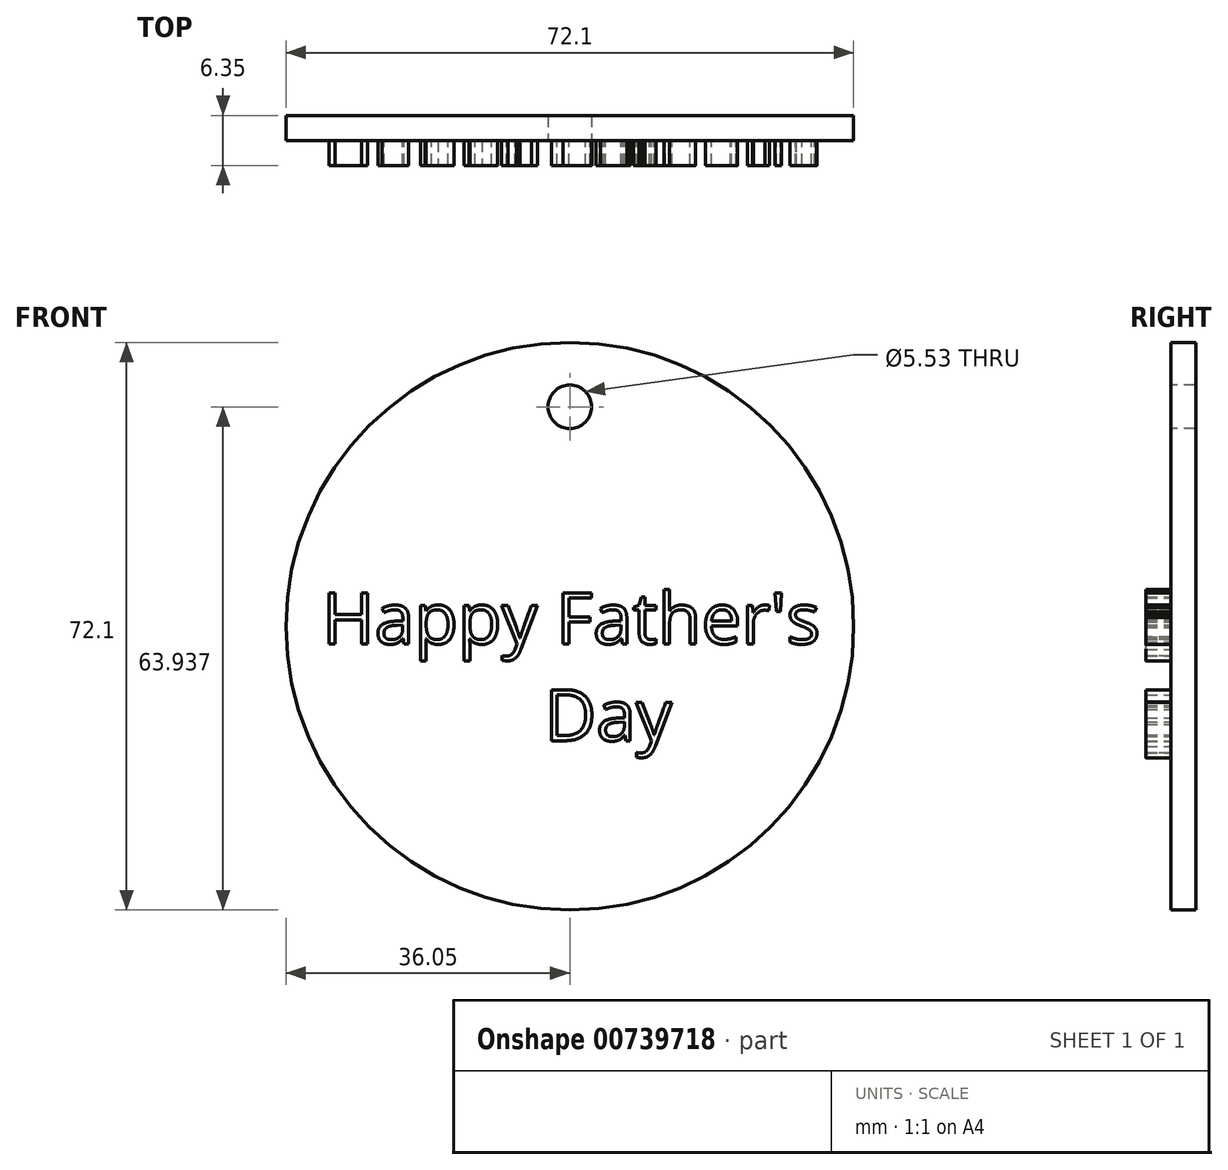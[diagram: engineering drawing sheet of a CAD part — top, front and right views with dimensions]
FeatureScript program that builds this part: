
annotation { "Feature Type Name" : "Feature", "Feature Type Description" : "" }
export const myFeature = defineFeature(function(context is Context, id is Id, definition is map)
    precondition{}
    {
        {
            var Q0;
            Q0=qCreatedBy(makeId("Front.planeOp"),FACE);
            var sketch = newSketch(context, id + "F0", { "sketchPlane" : qUnion([Q0])});
            skCircle(sketch, "E0", {"center": v(0, 0) * mm, "radius": 36.05 * mm});
            skSolve(sketch);
        }
        {
            var Q0;
            Q0=makeQuery(id+"F0.imprint","IMPRINT",FACE,{"disambiguationData":[TD([[makeQuery(id+"F0.imprint","IMPRINT",EDGE,{"derivedFrom":sQuery(id+"F0.wireOp",EDGE,"E0")}),1.0]])]});
            extrude(context, id + "F1", {"entities" : qUnion([Q0]), "depth" : 3.17 * mm, "offsetDistance" : 25.4 * mm});
        }
        {
            var Q0;
            Q0=makeQuery(id+"F1.opExtrude","CAP_FACE",FACE,{"disambiguationData":[OSD([sQuery(id+"F0.wireOp",EDGE,"E0")])],"isStart":false});
            var sketch = newSketch(context, id + "F2", { "sketchPlane" : qUnion([Q0])});
            skText(sketch, "E1", { "text": "Happy Father\'s\n            Day", "fontName": "OpenSans-Regular.ttf"});
            const initialGuessF2  = {"E1": [-0.03148, -0.00222, 1, 0, 0.00652]};
            skSetInitialGuess(sketch, initialGuessF2);
            skSolve(sketch);
        }
        {
            var Q0;
            Q0 = qSketchRegion(id + "F2", true);
            extrude(context, id + "F3", {"entities" : qUnion([Q0]), "operationType" : NewBodyOperationType.ADD, "depth" : 3.17 * mm, "offsetDistance" : 25.4 * mm});
        }
        {
            var Q0;
            {var subQ0=sQuery(id+"F0.wireOp",EDGE,"E0");Q0=makeQuery(id+"F3.boolean.opBoolean","SPLIT",FACE,{"disambiguationData":[TD([makeQuery(id+"F1.opExtrude","SWEPT_FACE",FACE,{"disambiguationData":[OSD([subQ0])]})])],"derivedFrom":makeQuery(id+"F1.opExtrude","CAP_FACE",FACE,{"disambiguationData":[OSD([subQ0])],"isStart":false})});}
            var sketch = newSketch(context, id + "F4", { "sketchPlane" : qUnion([Q0])});
            skCircle(sketch, "E2", {"center": v(0, 27.89) * mm, "radius": 2.77 * mm});
            skSolve(sketch);
        }
        {
            var Q0;
            Q0 = qSketchRegion(id + "F4", true);
            extrude(context, id + "F5", {"entities" : qUnion([Q0]), "operationType" : NewBodyOperationType.REMOVE, "endBound" : BoundingType.SYMMETRIC, "oppositeDirection" : true, "depth" : 25.4 * mm, "offsetDistance" : 25.4 * mm});
        }
    });
